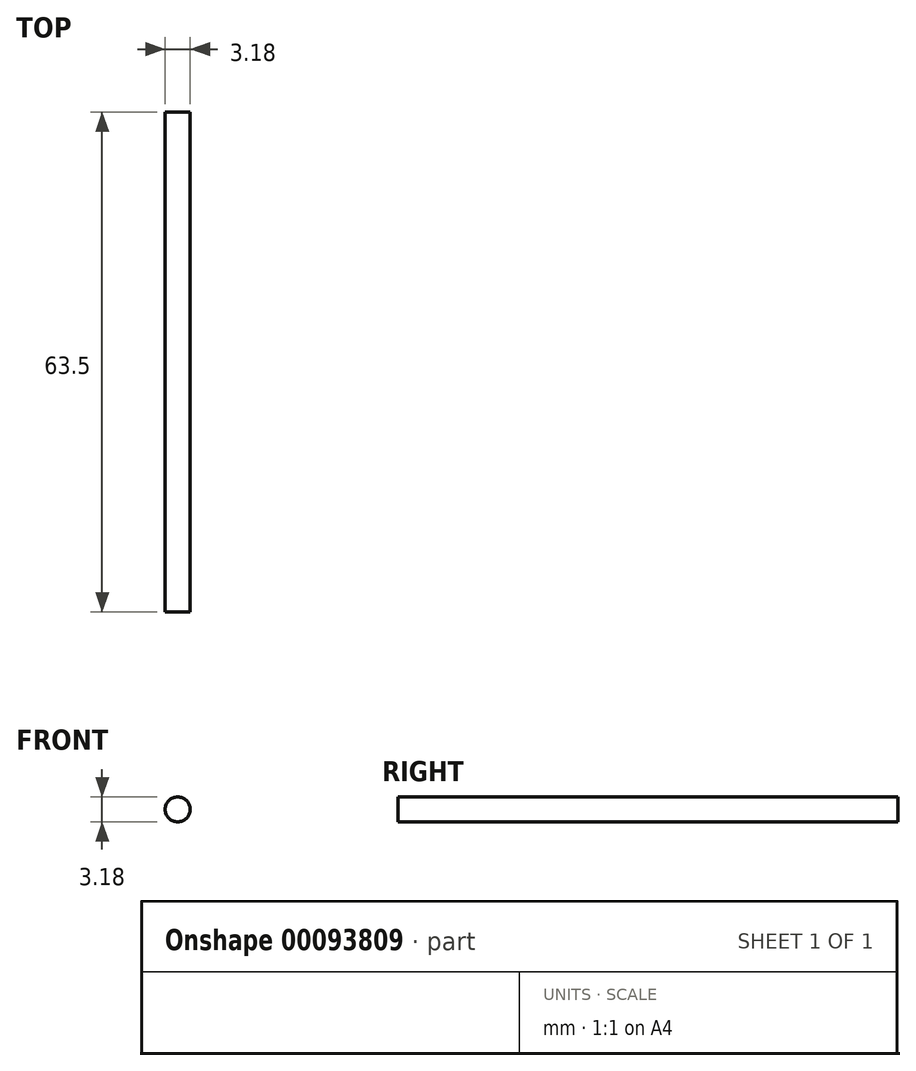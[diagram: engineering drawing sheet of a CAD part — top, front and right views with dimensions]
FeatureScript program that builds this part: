
annotation { "Feature Type Name" : "Feature", "Feature Type Description" : "" }
export const myFeature = defineFeature(function(context is Context, id is Id, definition is map)
    precondition{}
    {
        {
            var Q0;
            Q0=qCreatedBy(makeId("Front.planeOp"),FACE);
            var sketch = newSketch(context, id + "F0", { "sketchPlane" : qUnion([Q0])});
            skCircle(sketch, "E0", {"center": v(0, 0) * mm, "radius": 1.59 * mm});
            skSolve(sketch);
        }
        {
            var Q0;
            Q0 = qSketchRegion(id + "F0", true);
            extrude(context, id + "F1", {"entities" : qUnion([Q0]), "oppositeDirection" : true, "depth" : 63.5 * mm});
        }
    });
